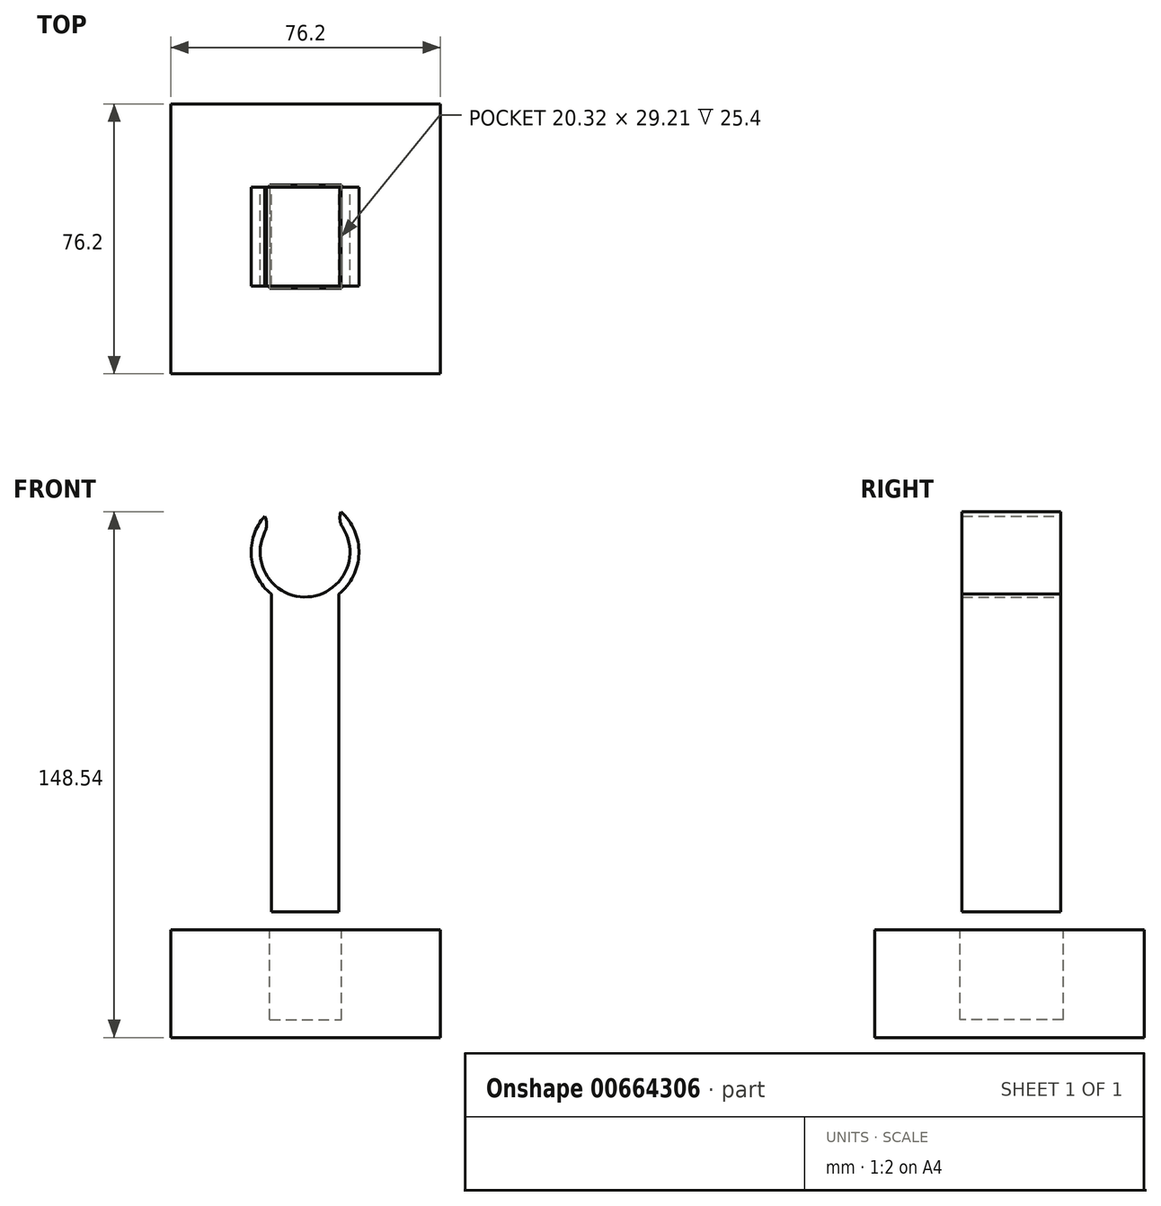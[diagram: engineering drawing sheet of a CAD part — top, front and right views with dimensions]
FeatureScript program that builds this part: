
annotation { "Feature Type Name" : "Feature", "Feature Type Description" : "" }
export const myFeature = defineFeature(function(context is Context, id is Id, definition is map)
    precondition{}
    {
        {
            var Q0;
            Q0=qCreatedBy(makeId("Front.planeOp"),FACE);
            var sketch = newSketch(context, id + "F0", { "sketchPlane" : qUnion([Q0])});
            skCircle(sketch, "E0", {"center": v(0, 0) * mm, "radius": 12.7 * mm});
            skCircle(sketch, "E1", {"center": v(0, 0) * mm, "radius": 15.24 * mm});
            skLineSegment(sketch, "E2", {"start": v(0, 0) * mm, "end": v(-16.77, 14.92) * mm});
            skLineSegment(sketch, "E3", {"start": v(0, 0) * mm, "end": v(12.99, 14.6) * mm});
            skLineSegment(sketch, "E4.bottom", {"start": v(-9.53, -11.9) * mm, "end": v(9.53, -11.9) * mm});
            skLineSegment(sketch, "E4.top", {"start": v(-9.53, -25.4) * mm, "end": v(9.53, -25.4) * mm});
            skLineSegment(sketch, "E4.left", {"start": v(-9.53, -11.9) * mm, "end": v(-9.53, -25.4) * mm});
            skLineSegment(sketch, "E4.right", {"start": v(9.53, -11.9) * mm, "end": v(9.53, -25.4) * mm});
            skSolve(sketch);
        }
        {
            var Q0;
            {var subQ0=sQuery(id+"F0.wireOp",EDGE,"E2");var subQ1=sQuery(id+"F0.wireOp",EDGE,"E0");var subQ2=makeQuery(id+"F0.imprint","INTERSECT",VERTEX,{"derivedFrom":[subQ1,subQ0]});Q0=makeQuery(id+"F0.imprint","IMPRINT",FACE,{"disambiguationData":[TD([[makeQuery(id+"F0.imprint","IMPRINT",EDGE,{"disambiguationData":[TD([[subQ2,-1.0]])],"derivedFrom":subQ1}),-1.0]])]});}
            var Q1;
            {var subQ0=sQuery(id+"F0.wireOp",EDGE,"E4.bottom");var subQ1=sQuery(id+"F0.wireOp",EDGE,"E0");var subQ2=makeQuery(id+"F0.imprint","INTERSECT",VERTEX,{"disambiguationData":[OD(0.0)],"derivedFrom":[subQ1,subQ0]});Q1=makeQuery(id+"F0.imprint","IMPRINT",FACE,{"disambiguationData":[TD([[makeQuery(id+"F0.imprint","IMPRINT",EDGE,{"disambiguationData":[TD([[subQ2,-1.0]])],"derivedFrom":subQ1}),-1.0]])]});}
            var Q2;
            Q2=makeQuery(id+"F0.imprint","IMPRINT",FACE,{"disambiguationData":[TD([[makeQuery(id+"F0.imprint","IMPRINT",EDGE,{"derivedFrom":sQuery(id+"F0.wireOp",EDGE,"E4.top")}),1.0]])]});
            var Q3;
            {var subQ0=sQuery(id+"F0.wireOp",EDGE,"E3");var subQ1=sQuery(id+"F0.wireOp",EDGE,"E0");var subQ2=makeQuery(id+"F0.imprint","INTERSECT",VERTEX,{"derivedFrom":[subQ1,subQ0]});Q3=makeQuery(id+"F0.imprint","IMPRINT",FACE,{"disambiguationData":[TD([[makeQuery(id+"F0.imprint","IMPRINT",EDGE,{"disambiguationData":[TD([[subQ2,1.0]])],"derivedFrom":subQ1}),-1.0]])]});}
            var Q4;
            {var subQ0=sQuery(id+"F0.wireOp",EDGE,"E4.bottom");var subQ1=sQuery(id+"F0.wireOp",EDGE,"E0");var subQ2=makeQuery(id+"F0.imprint","INTERSECT",VERTEX,{"disambiguationData":[OD(0.0)],"derivedFrom":[subQ1,subQ0]});Q4=makeQuery(id+"F0.imprint","IMPRINT",FACE,{"disambiguationData":[TD([[makeQuery(id+"F0.imprint","IMPRINT",EDGE,{"disambiguationData":[TD([[subQ2,1.0]])],"derivedFrom":subQ1}),-1.0]])]});}
            extrude(context, id + "F1", {"entities" : qUnion([Q0, Q1, Q2, Q3, Q4]), "depth" : 27.94 * mm, "offsetDistance" : 25.4 * mm});
        }
        {
            var Q0;
            Q0=makeQuery(id+"F1.opExtrude","SWEPT_FACE",FACE,{"disambiguationData":[OSD([sQuery(id+"F0.wireOp",EDGE,"E4.top")])]});
            var sketch = newSketch(context, id + "F2", { "sketchPlane" : qUnion([Q0])});
            skSolve(sketch);
        }
        {
            var Q0;
            {var subQ0=sQuery(id+"F0.wireOp",EDGE,"E4.top");Q0=makeQuery(id+"F2.imprint","IMPRINT",FACE,{"disambiguationData":[TD([[makeQuery(id+"F2.imprint","IMPRINT",EDGE,{"derivedFrom":makeQuery(id+"F1.opExtrude","CAP_EDGE",EDGE,{"disambiguationData":[OSD([subQ0])],"isStart":true})}),1.0]])]});}
            var Q1;
            Q1=makeQuery(id+"F2.imprint","IMPRINT",FACE,{"disambiguationData":[TD([[makeQuery(id+"F2.imprint","IMPRINT",EDGE,{"derivedFrom":sQuery(id+"F2.wireOp",EDGE,"9jxceJ7P-KJ6h-T7AF-4Eiu-I0iuLIwrlJvw")}),1.0]])]});
            var Q2;
            {var subQ0=sQuery(id+"F2.wireOp",EDGE,"9jxceJ7P-KJ6h-T7AF-4Eiu-I0iuLIwrlJvw");var subQ1=sQuery(id+"F0.wireOp",EDGE,"E4.top");var subQ2=makeQuery(id+"F1.opExtrude","CAP_EDGE",EDGE,{"disambiguationData":[OSD([subQ1])],"isStart":false});var subQ3=makeQuery(id+"F2.imprint","INTERSECT",VERTEX,{"disambiguationData":[OD(1.0)],"derivedFrom":[subQ2,subQ0]});Q2=makeQuery(id+"F2.imprint","IMPRINT",FACE,{"disambiguationData":[TD([[makeQuery(id+"F2.imprint","IMPRINT",EDGE,{"disambiguationData":[TD([[subQ3,-1.0]])],"derivedFrom":subQ0}),-1.0]])]});}
            var Q3;
            {var subQ0=sQuery(id+"F2.wireOp",EDGE,"9jxceJ7P-KJ6h-T7AF-4Eiu-I0iuLIwrlJvw");var subQ1=sQuery(id+"F0.wireOp",EDGE,"E4.top");var subQ2=makeQuery(id+"F1.opExtrude","CAP_EDGE",EDGE,{"disambiguationData":[OSD([subQ1])],"isStart":false});var subQ3=makeQuery(id+"F2.imprint","INTERSECT",VERTEX,{"disambiguationData":[OD(0.0)],"derivedFrom":[subQ2,subQ0]});Q3=makeQuery(id+"F2.imprint","IMPRINT",FACE,{"disambiguationData":[TD([[makeQuery(id+"F2.imprint","IMPRINT",EDGE,{"disambiguationData":[TD([[subQ3,1.0]])],"derivedFrom":subQ0}),-1.0]])]});}
            var Q4;
            Q4=sQuery(id+"F2.wireOp",EDGE,"9jxceJ7P-KJ6h-T7AF-4Eiu-I0iuLIwrlJvw");
            extrude(context, id + "F3", {"entities" : qUnion([Q0, Q1, Q2, Q3]), "operationType" : NewBodyOperationType.ADD, "surfaceEntities" : qUnion([Q4]), "depth" : 50.8 * mm, "offsetDistance" : 25.4 * mm});
        }
        {
            var Q0;
            Q0=makeQuery(id+"F1.opExtrude","SWEPT_EDGE",EDGE,{"disambiguationData":[OSD([sQuery(id+"F0.wireOp",EDGE,"E0"),sQuery(id+"F0.wireOp",EDGE,"E2")])]});
            var Q1;
            Q1=makeQuery(id+"F1.opExtrude","SWEPT_EDGE",EDGE,{"disambiguationData":[OSD([sQuery(id+"F0.wireOp",EDGE,"E0"),sQuery(id+"F0.wireOp",EDGE,"E3")])]});
            fillet(context, id + "F4", {"entities" : qUnion([Q0, Q1]), "radius" : 5.08 * mm, "tangentPropagation" : true, "allowEdgeOverflow" : false});
        }
        {
            var Q0;
            {var subQ0=sQuery(id+"F2.wireOp",EDGE,"9jxceJ7P-KJ6h-T7AF-4Eiu-I0iuLIwrlJvw");var subQ1=sQuery(id+"F0.wireOp",EDGE,"E4.top");var subQ3=sQuery(id+"F0.wireOp",EDGE,"E4.right");var subQ5=sQuery(id+"F0.wireOp",EDGE,"E4.left");Q0=makeQuery(id+"FxMVe1Hk4JVnxUn_1.boolean.opBoolean","SPLIT",FACE,{"disambiguationData":[TD([makeQuery(id+"F1.opExtrude","SWEPT_FACE",FACE,{"disambiguationData":[OSD([subQ5])]})])],"derivedFrom":makeQuery(id+"F3.opExtrude","CAP_FACE",FACE,{"disambiguationData":[OSD([subQ1,subQ5,subQ3,subQ0])],"isStart":false})});}
            var Q1;
            {var subQ0=sQuery(id+"F2.wireOp",EDGE,"9jxceJ7P-KJ6h-T7AF-4Eiu-I0iuLIwrlJvw");var subQ1=sQuery(id+"F0.wireOp",EDGE,"E4.top");var subQ3=sQuery(id+"F0.wireOp",EDGE,"E4.right");var subQ5=sQuery(id+"F0.wireOp",EDGE,"E4.left");Q1=makeQuery(id+"FxMVe1Hk4JVnxUn_1.boolean.opBoolean","SPLIT",FACE,{"disambiguationData":[TD([makeQuery(id+"F1.opExtrude","SWEPT_FACE",FACE,{"disambiguationData":[OSD([subQ3])]})])],"derivedFrom":makeQuery(id+"F3.opExtrude","CAP_FACE",FACE,{"disambiguationData":[OSD([subQ1,subQ5,subQ3,subQ0])],"isStart":false})});}
            extrude(context, id + "F5", {"entities" : qUnion([Q0, Q1]), "operationType" : NewBodyOperationType.ADD, "depth" : 25.4 * mm, "offsetDistance" : 25.4 * mm});
        }
        {
            var Q0;
            Q0=makeQuery(id+"F5.opExtrude","CAP_FACE",FACE,{"disambiguationData":[OSD([sQuery(id+"F0.wireOp",EDGE,"E4.top"),sQuery(id+"F0.wireOp",EDGE,"E4.left"),sQuery(id+"F0.wireOp",EDGE,"E4.right")])],"isStart":false});
            cPlane(context, id + "F6", {"entities" : qUnion([Q0]), "cplaneType" : CPlaneType.OFFSET, "offset" : 5.08 * mm, "width" : 152.4 * mm, "height" : 152.4 * mm});
        }
        {
            var Q0;
            Q0=qCreatedBy(id+"F6.planeOp",FACE);
            var sketch = newSketch(context, id + "F7", { "sketchPlane" : qUnion([Q0])});
            skLineSegment(sketch, "E5.bottom", {"start": v(-10.01, -0.7) * mm, "end": v(10.3, -0.7) * mm});
            skLineSegment(sketch, "E5.top", {"start": v(-10.01, 28.51) * mm, "end": v(10.3, 28.51) * mm});
            skLineSegment(sketch, "E5.left", {"start": v(-10.01, -0.7) * mm, "end": v(-10.01, 28.51) * mm});
            skLineSegment(sketch, "E5.right", {"start": v(10.3, -0.7) * mm, "end": v(10.3, 28.51) * mm});
            skLineSegment(sketch, "E6.bottom", {"start": v(-37.95, -23.56) * mm, "end": v(38.25, -23.56) * mm});
            skLineSegment(sketch, "E6.top", {"start": v(-37.95, 52.64) * mm, "end": v(38.25, 52.64) * mm});
            skLineSegment(sketch, "E6.left", {"start": v(-37.95, -23.56) * mm, "end": v(-37.95, 52.64) * mm});
            skLineSegment(sketch, "E6.right", {"start": v(38.25, -23.56) * mm, "end": v(38.25, 52.64) * mm});
            skSolve(sketch);
        }
        {
            var Q0;
            Q0=makeQuery(id+"F7.imprint","IMPRINT",FACE,{"disambiguationData":[TD([[makeQuery(id+"F7.imprint","IMPRINT",EDGE,{"derivedFrom":sQuery(id+"F7.wireOp",EDGE,"E5.bottom")}),-1.0]])]});
            extrude(context, id + "F8", {"entities" : qUnion([Q0]), "depth" : 25.4 * mm, "offsetDistance" : 25.4 * mm});
        }
        {
            var Q0;
            Q0=makeQuery(id+"F8.opExtrude","CAP_FACE",FACE,{"disambiguationData":[OSD([sQuery(id+"F7.wireOp",EDGE,"E5.bottom"),sQuery(id+"F7.wireOp",EDGE,"E5.top"),sQuery(id+"F7.wireOp",EDGE,"E5.left"),sQuery(id+"F7.wireOp",EDGE,"E5.right"),sQuery(id+"F7.wireOp",EDGE,"E6.bottom"),sQuery(id+"F7.wireOp",EDGE,"E6.top"),sQuery(id+"F7.wireOp",EDGE,"E6.left"),sQuery(id+"F7.wireOp",EDGE,"E6.right")])],"isStart":false});
            var sketch = newSketch(context, id + "F9", { "sketchPlane" : qUnion([Q0])});
            skLineSegment(sketch, "E7.bottom", {"start": v(-37.95, -23.56) * mm, "end": v(38.25, -23.56) * mm});
            skLineSegment(sketch, "E7.top", {"start": v(-37.95, 52.64) * mm, "end": v(38.25, 52.64) * mm});
            skLineSegment(sketch, "E7.left", {"start": v(-37.95, -23.56) * mm, "end": v(-37.95, 52.64) * mm});
            skLineSegment(sketch, "E7.right", {"start": v(38.25, -23.56) * mm, "end": v(38.25, 52.64) * mm});
            skSolve(sketch);
        }
        {
            var Q0;
            Q0 = qSketchRegion(id + "F9", true);
            extrude(context, id + "F10", {"entities" : qUnion([Q0]), "operationType" : NewBodyOperationType.ADD, "depth" : 5.08 * mm, "offsetDistance" : 25.4 * mm});
        }
    });
